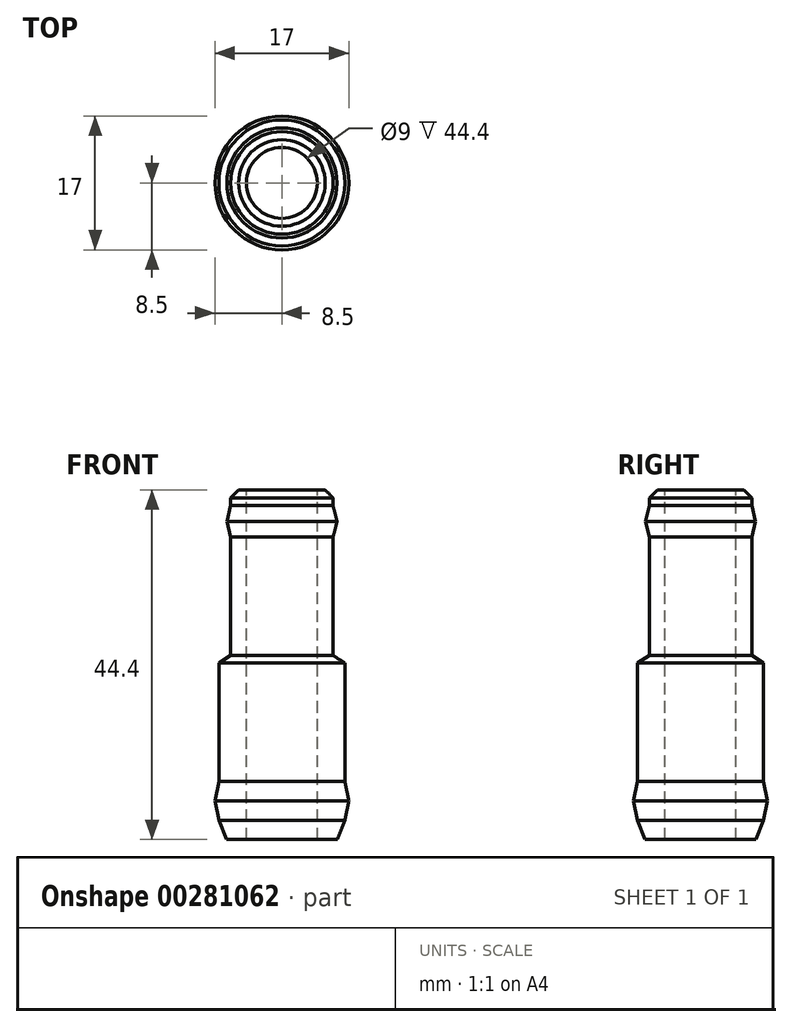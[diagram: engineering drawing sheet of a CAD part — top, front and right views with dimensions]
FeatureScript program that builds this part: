
annotation { "Feature Type Name" : "Feature", "Feature Type Description" : "" }
export const myFeature = defineFeature(function(context is Context, id is Id, definition is map)
    precondition{}
    {
        {
            var Q0;
            Q0=qCreatedBy(makeId("Front.planeOp"),FACE);
            var sketch = newSketch(context, id + "F0", { "sketchPlane" : qUnion([Q0])});
            skLineSegment(sketch, "E0", {"start": v(-4.5, 25.4) * mm, "end": v(-4.5, -19) * mm});
            skLineSegment(sketch, "E1", {"start": v(-4.5, 25.4) * mm, "end": v(-6.5, 25.4) * mm});
            skLineSegment(sketch, "E2", {"start": v(-6.5, 25.4) * mm, "end": v(-6.5, 23.4) * mm});
            skLineSegment(sketch, "E3", {"start": v(-6.5, 23.4) * mm, "end": v(-7, 21.4) * mm});
            skLineSegment(sketch, "E4", {"start": v(-7, 21.4) * mm, "end": v(-6.5, 19.4) * mm});
            skLineSegment(sketch, "E5", {"start": v(-6.5, 19.4) * mm, "end": v(-6.5, 4.4) * mm});
            skLineSegment(sketch, "E6", {"start": v(-8, 3.4) * mm, "end": v(-8, -11.6) * mm});
            skLineSegment(sketch, "E7", {"start": v(-8, -11.6) * mm, "end": v(-8.5, -14.1) * mm});
            skLineSegment(sketch, "E8", {"start": v(-8.5, -14.1) * mm, "end": v(-8, -16.6) * mm});
            skLineSegment(sketch, "E9", {"start": v(-8, -16.6) * mm, "end": v(-7.03, -19) * mm});
            skLineSegment(sketch, "E10", {"start": v(-7.03, -19) * mm, "end": v(-4.5, -19) * mm});
            skLineSegment(sketch, "E11", {"start": v(-6.5, 4.4) * mm, "end": v(-8, 3.4) * mm});
            skLineSegment(sketch, "E12", {"start": v(0, 11.4) * mm, "end": v(0, -17.88) * mm, "construction": true});
            skSolve(sketch);
        }
        {
            var Q0;
            Q0=makeQuery(id+"F0.imprint","IMPRINT",FACE,{"disambiguationData":[TD([[makeQuery(id+"F0.imprint","IMPRINT",EDGE,{"derivedFrom":sQuery(id+"F0.wireOp",EDGE,"E0")}),-1.0]])]});
            var Q1;
            Q1=sQuery(id+"F0.wireOp",EDGE,"E12");
            revolve(context, id + "F1", {"entities" : qUnion([Q0]), "axis" : qUnion([Q1]), "revolveType" : RevolveType.FULL});
        }
        {
            var Q0;
            Q0=makeQuery(id+"F1.opRevolve","SWEPT_EDGE",EDGE,{"disambiguationData":[OSD([sQuery(id+"F0.wireOp",EDGE,"E1"),sQuery(id+"F0.wireOp",EDGE,"E2")])]});
            chamfer(context, id + "F2", {"entities" : qUnion([Q0]), "width" : 1 * mm, "tangentPropagation" : true});
        }
    });
